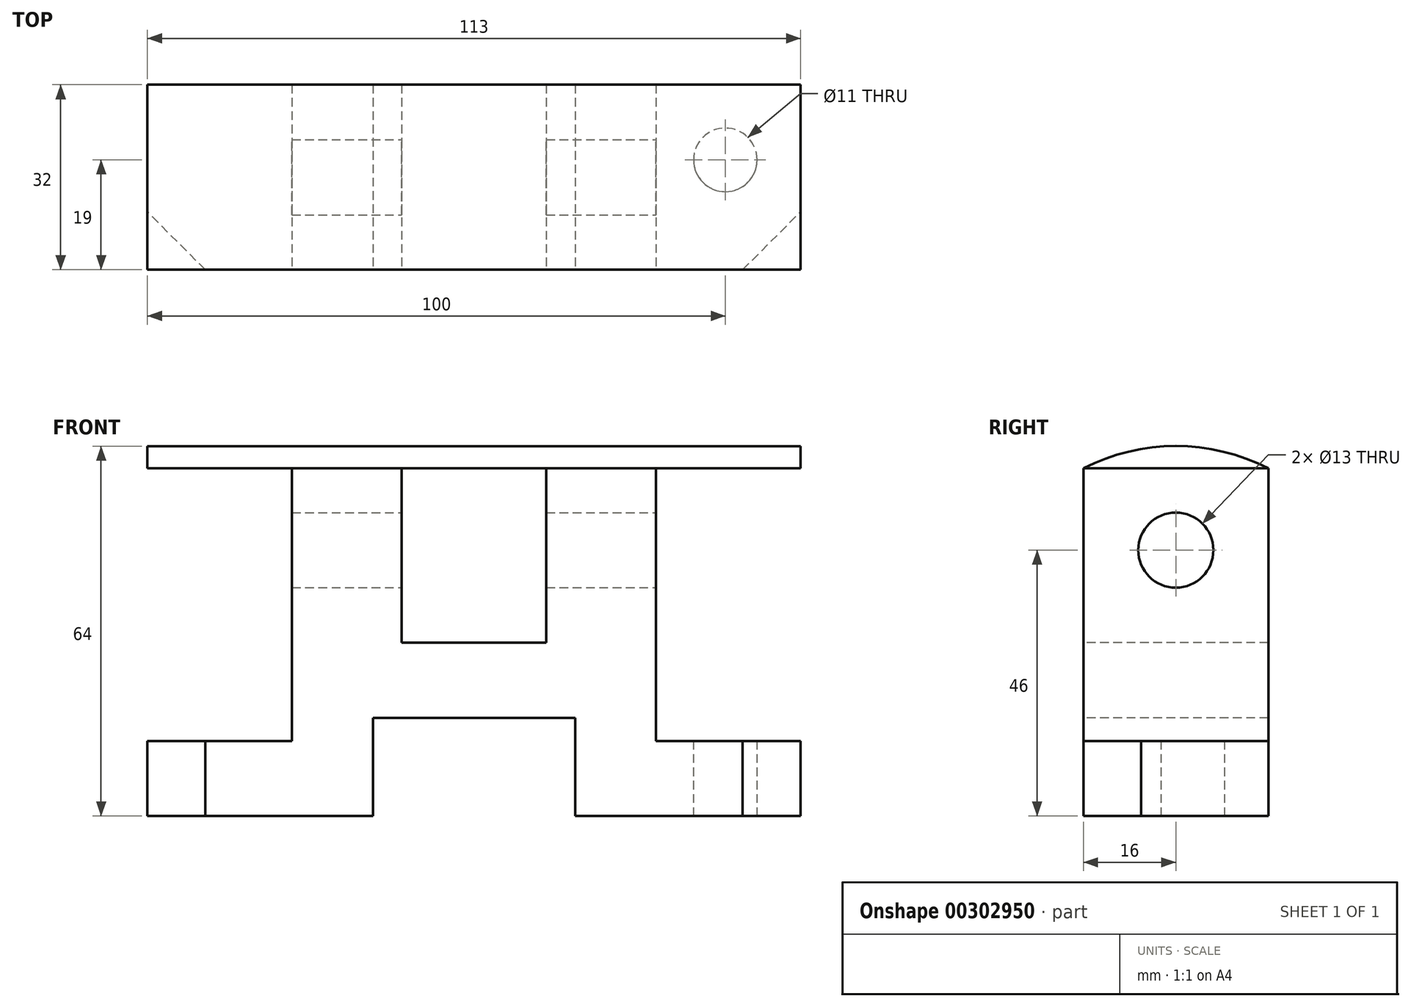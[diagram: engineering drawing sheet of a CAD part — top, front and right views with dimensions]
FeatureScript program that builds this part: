
annotation { "Feature Type Name" : "Feature", "Feature Type Description" : "" }
export const myFeature = defineFeature(function(context is Context, id is Id, definition is map)
    precondition{}
    {
        {
            var Q0;
            Q0=qCreatedBy(makeId("Right.planeOp"),FACE);
            var sketch = newSketch(context, id + "F0", { "sketchPlane" : qUnion([Q0])});
            skLineSegment(sketch, "E0", {"start": v(0, 0) * mm, "end": v(16, 0) * mm});
            skLineSegment(sketch, "E1", {"start": v(0, 0) * mm, "end": v(-16, 0) * mm});
            skArc(sketch, "E2", {"start": v(16, 60.13) * mm, "mid": v(0, 64) * mm, "end": v(-16, 60.13) * mm});
            skLineSegment(sketch, "E3", {"start": v(-16, 0) * mm, "end": v(-16, 60.13) * mm});
            skLineSegment(sketch, "E4", {"start": v(16, 0) * mm, "end": v(16, 60.13) * mm});
            skSolve(sketch);
        }
        {
            var Q0;
            Q0=makeQuery(id+"F0.imprint","IMPRINT",FACE,{"disambiguationData":[TD([[makeQuery(id+"F0.imprint","IMPRINT",EDGE,{"derivedFrom":sQuery(id+"F0.wireOp",EDGE,"E0")}),1.0]])]});
            extrude(context, id + "F1", {"entities" : qUnion([Q0]), "endBound" : BoundingType.SYMMETRIC, "depth" : 113 * mm});
        }
        {
            var Q0;
            Q0=makeQuery(id+"F1.opExtrude","SWEPT_FACE",FACE,{"disambiguationData":[OSD([sQuery(id+"F0.wireOp",EDGE,"E3")])]});
            var sketch = newSketch(context, id + "F2", { "sketchPlane" : qUnion([Q0])});
            skLineSegment(sketch, "E5.0.0", {"start": v(-56.5, 64) * mm, "end": v(-56.5, 0) * mm});
            skLineSegment(sketch, "E5.0.1", {"start": v(-56.5, 0) * mm, "end": v(56.5, 0) * mm});
            skLineSegment(sketch, "E5.0.2", {"start": v(56.5, 0) * mm, "end": v(56.5, 64) * mm});
            skLineSegment(sketch, "E5.0.3", {"start": v(56.5, 60.13) * mm, "end": v(-56.5, 60.13) * mm});
            skLineSegment(sketch, "E6", {"start": v(0, 0) * mm, "end": v(-17.5, 0) * mm, "construction": true});
            skLineSegment(sketch, "E7", {"start": v(-17.5, 0) * mm, "end": v(-17.5, 17) * mm});
            skLineSegment(sketch, "E8", {"start": v(-17.5, 17) * mm, "end": v(17.5, 17) * mm});
            skLineSegment(sketch, "E9", {"start": v(17.5, 17) * mm, "end": v(17.5, 0) * mm});
            skLineSegment(sketch, "E10", {"start": v(17.5, 0) * mm, "end": v(-17.5, 0) * mm});
            skLineSegment(sketch, "E11", {"start": v(-56.5, 64) * mm, "end": v(56.5, 64) * mm});
            skLineSegment(sketch, "E12.bottom", {"start": v(-56.5, 64) * mm, "end": v(-31.5, 64) * mm});
            skLineSegment(sketch, "E12.top", {"start": v(-56.5, 13) * mm, "end": v(-31.5, 13) * mm});
            skLineSegment(sketch, "E12.left", {"start": v(-56.5, 64) * mm, "end": v(-56.5, 13) * mm});
            skLineSegment(sketch, "E12.right", {"start": v(-31.5, 64) * mm, "end": v(-31.5, 13) * mm});
            skLineSegment(sketch, "E13.MirrorCS", {"start": v(31.5, 64) * mm, "end": v(31.5, 13) * mm});
            skLineSegment(sketch, "E14.MirrorCS", {"start": v(56.5, 13) * mm, "end": v(31.5, 13) * mm});
            skLineSegment(sketch, "E15.MirrorCS", {"start": v(56.5, 64) * mm, "end": v(31.5, 64) * mm});
            skLineSegment(sketch, "E16", {"start": v(0, 17) * mm, "end": v(0, 30) * mm, "construction": true});
            skLineSegment(sketch, "E17", {"start": v(0, 30) * mm, "end": v(12.5, 30) * mm});
            skLineSegment(sketch, "E18", {"start": v(12.5, 30) * mm, "end": v(12.5, 64) * mm});
            skLineSegment(sketch, "E19", {"start": v(12.5, 64) * mm, "end": v(-12.5, 64) * mm});
            skLineSegment(sketch, "E20", {"start": v(-12.5, 64) * mm, "end": v(-12.5, 30) * mm});
            skLineSegment(sketch, "E21", {"start": v(-12.5, 30) * mm, "end": v(0, 30) * mm});
            skSolve(sketch);
        }
        {
            var Q0;
            {var subQ5=sQuery(id+"F2.wireOp",EDGE,"E12.top");Q0=makeQuery(id+"F2.imprint","IMPRINT",FACE,{"disambiguationData":[TD([[makeQuery(id+"F2.imprint","IMPRINT",EDGE,{"derivedFrom":subQ5}),1.0]])]});}
            var Q1;
            {var subQ5=sQuery(id+"F2.wireOp",EDGE,"E12.bottom");Q1=makeQuery(id+"F2.imprint","IMPRINT",FACE,{"disambiguationData":[TD([[makeQuery(id+"F2.imprint","IMPRINT",EDGE,{"derivedFrom":subQ5}),-1.0]])]});}
            var Q2;
            {var subQ4=sQuery(id+"F2.wireOp",EDGE,"E17");Q2=makeQuery(id+"F2.imprint","IMPRINT",FACE,{"disambiguationData":[TD([[makeQuery(id+"F2.imprint","IMPRINT",EDGE,{"derivedFrom":subQ4}),1.0]])]});}
            var Q3;
            {var subQ5=sQuery(id+"F2.wireOp",EDGE,"E19");Q3=makeQuery(id+"F2.imprint","IMPRINT",FACE,{"disambiguationData":[TD([[makeQuery(id+"F2.imprint","IMPRINT",EDGE,{"derivedFrom":subQ5}),1.0]])]});}
            var Q4;
            {var subQ3=sQuery(id+"F2.wireOp",EDGE,"E14.MirrorCS");Q4=makeQuery(id+"F2.imprint","IMPRINT",FACE,{"disambiguationData":[TD([[makeQuery(id+"F2.imprint","IMPRINT",EDGE,{"derivedFrom":subQ3}),-1.0]])]});}
            var Q5;
            {var subQ3=sQuery(id+"F2.wireOp",EDGE,"E15.MirrorCS");Q5=makeQuery(id+"F2.imprint","IMPRINT",FACE,{"disambiguationData":[TD([[makeQuery(id+"F2.imprint","IMPRINT",EDGE,{"derivedFrom":subQ3}),1.0]])]});}
            var Q6;
            Q6=makeQuery(id+"F2.imprint","IMPRINT",FACE,{"disambiguationData":[TD([[makeQuery(id+"F2.imprint","IMPRINT",EDGE,{"derivedFrom":sQuery(id+"F2.wireOp",EDGE,"E7")}),-1.0]])]});
            extrude(context, id + "F3", {"entities" : qUnion([Q0, Q1, Q2, Q3, Q4, Q5, Q6]), "operationType" : NewBodyOperationType.REMOVE, "oppositeDirection" : true, "depth" : 50 * mm});
        }
        {
            var Q0;
            Q0=makeQuery(id+"F3.boolean.opBoolean","COPY",FACE,{"derivedFrom":makeQuery(id+"F3.opExtrude","SWEPT_FACE",FACE,{"disambiguationData":[OSD([sQuery(id+"F2.wireOp",EDGE,"E13.MirrorCS")])]})});
            var sketch = newSketch(context, id + "F4", { "sketchPlane" : qUnion([Q0])});
            skLineSegment(sketch, "E22.0.0", {"start": v(16, 13) * mm, "end": v(16, 60.13) * mm});
            skArc(sketch, "E22.0.1", {"start": v(16, 60.13) * mm, "mid": v(0, 64) * mm, "end": v(-16, 60.13) * mm});
            skLineSegment(sketch, "E22.0.2", {"start": v(-16, 60.13) * mm, "end": v(-16, 13) * mm});
            skLineSegment(sketch, "E22.0.3", {"start": v(-16, 13) * mm, "end": v(16, 13) * mm});
            skCircle(sketch, "E23", {"center": v(0, 46) * mm, "radius": 6.5 * mm});
            skSolve(sketch);
        }
        {
            var Q0;
            Q0=makeQuery(id+"F4.imprint","IMPRINT",FACE,{"disambiguationData":[TD([[makeQuery(id+"F4.imprint","IMPRINT",EDGE,{"derivedFrom":sQuery(id+"F4.wireOp",EDGE,"E23")}),1.0]])]});
            extrude(context, id + "F5", {"entities" : qUnion([Q0]), "operationType" : NewBodyOperationType.REMOVE, "oppositeDirection" : true, "depth" : 113 * mm});
        }
        {
            var Q0;
            Q0=makeQuery(id+"F3.boolean.opBoolean","COPY",FACE,{"derivedFrom":makeQuery(id+"F3.opExtrude","SWEPT_FACE",FACE,{"disambiguationData":[OSD([sQuery(id+"F2.wireOp",EDGE,"E14.MirrorCS")])]})});
            var sketch = newSketch(context, id + "F6", { "sketchPlane" : qUnion([Q0])});
            skCircle(sketch, "E24", {"center": v(43.5, 3) * mm, "radius": 5.5 * mm});
            skCircle(sketch, "E25.MirrorC", {"center": v(-43.5, 3) * mm, "radius": 5.5 * mm});
            skSolve(sketch);
        }
        {
            var Q0;
            Q0=makeQuery(id+"F6.imprint","IMPRINT",FACE,{"disambiguationData":[TD([[makeQuery(id+"F6.imprint","IMPRINT",EDGE,{"derivedFrom":sQuery(id+"F6.wireOp",EDGE,"E25.MirrorC")}),-1.0]])]});
            var Q1;
            Q1=makeQuery(id+"F6.imprint","IMPRINT",FACE,{"disambiguationData":[TD([[makeQuery(id+"F6.imprint","IMPRINT",EDGE,{"derivedFrom":sQuery(id+"F6.wireOp",EDGE,"E24")}),1.0]])]});
            extrude(context, id + "F7", {"entities" : qUnion([Q0, Q1]), "operationType" : NewBodyOperationType.REMOVE, "oppositeDirection" : true, "depth" : 25 * mm});
        }
        {
            var Q0;
            Q0=makeQuery(id+"F1.opExtrude","CAP_EDGE",EDGE,{"disambiguationData":[OSD([sQuery(id+"F0.wireOp",EDGE,"E3")])],"isStart":true});
            var Q1;
            Q1=makeQuery(id+"F1.opExtrude","CAP_EDGE",EDGE,{"disambiguationData":[OSD([sQuery(id+"F0.wireOp",EDGE,"E3")])],"isStart":false});
            chamfer(context, id + "F8", {"entities" : qUnion([Q0, Q1]), "chamferType" : ChamferType.OFFSET_ANGLE, "width" : 10 * mm, "oppositeDirection" : false, "angle" : 45 * degree, "tangentPropagation" : true});
        }
    });
